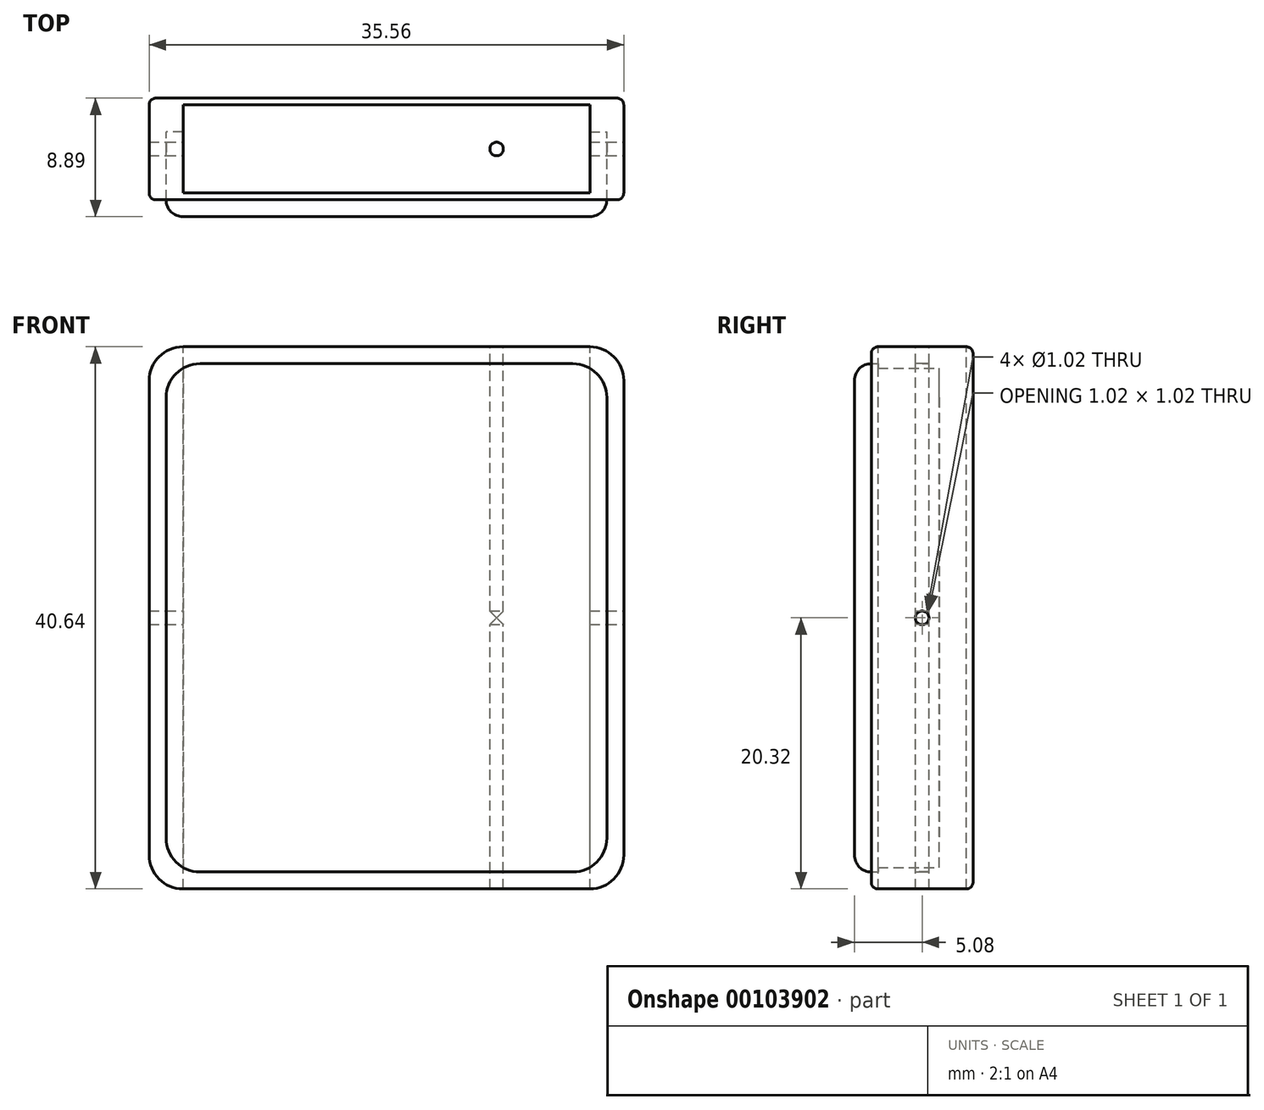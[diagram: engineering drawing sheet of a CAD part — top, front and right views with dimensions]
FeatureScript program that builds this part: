
annotation { "Feature Type Name" : "Feature", "Feature Type Description" : "" }
export const myFeature = defineFeature(function(context is Context, id is Id, definition is map)
    precondition{}
    {
        {
            var Q0;
            Q0=qCreatedBy(makeId("Front.planeOp"),FACE);
            var sketch = newSketch(context, id + "F0", { "sketchPlane" : qUnion([Q0])});
            skLineSegment(sketch, "E0.bottom", {"start": v(-17.78, -20.32) * mm, "end": v(17.78, -20.32) * mm});
            skLineSegment(sketch, "E0.top", {"start": v(-17.78, 20.32) * mm, "end": v(17.78, 20.32) * mm});
            skLineSegment(sketch, "E0.left", {"start": v(-17.78, -20.32) * mm, "end": v(-17.78, 20.32) * mm});
            skLineSegment(sketch, "E0.right", {"start": v(17.78, -20.32) * mm, "end": v(17.78, 20.32) * mm});
            skPoint(sketch, "E0.middle", {"position": v(0, 0) * mm});
            skSolve(sketch);
        }
        {
            var Q0;
            Q0=makeQuery(id+"F0.imprint","IMPRINT",FACE,{"disambiguationData":[TD([[makeQuery(id+"F0.imprint","IMPRINT",EDGE,{"derivedFrom":sQuery(id+"F0.wireOp",EDGE,"E0.bottom")}),1.0]])]});
            extrude(context, id + "F1", {"entities" : qUnion([Q0]), "depth" : 3.8 * mm, "hasSecondDirection" : true, "secondDirectionOppositeDirection" : true, "secondDirectionDepth" : 3.8 * mm});
        }
        {
            var Q0;
            Q0=makeQuery(id+"F1.opExtrude","CAP_FACE",FACE,{"disambiguationData":[OSD([sQuery(id+"F0.wireOp",EDGE,"E0.bottom"),sQuery(id+"F0.wireOp",EDGE,"E0.top"),sQuery(id+"F0.wireOp",EDGE,"E0.left"),sQuery(id+"F0.wireOp",EDGE,"E0.right")])],"isStart":false});
            var sketch = newSketch(context, id + "F2", { "sketchPlane" : qUnion([Q0])});
            skLineSegment(sketch, "E1.bottom", {"start": v(-13.97, 19.05) * mm, "end": v(13.97, 19.05) * mm});
            skLineSegment(sketch, "E1.top", {"start": v(-13.97, -19.05) * mm, "end": v(13.97, -19.05) * mm});
            skLineSegment(sketch, "E1.left", {"start": v(-16.51, 16.51) * mm, "end": v(-16.51, -16.51) * mm});
            skLineSegment(sketch, "E1.right", {"start": v(16.51, 16.51) * mm, "end": v(16.51, -16.51) * mm});
            skPoint(sketch, "E1.middle", {"position": v(0, 0) * mm});
            skPoint(sketch, "E2.visualSharp", {"position": v(16.51, 19.05) * mm});
            skArc(sketch, "E2.filletArc", {"start": v(16.51, 16.51) * mm, "mid": v(15.77, 18.3) * mm, "end": v(13.97, 19.05) * mm});
            skPoint(sketch, "E3.visualSharp", {"position": v(-16.51, 19.05) * mm});
            skArc(sketch, "E3.filletArc", {"start": v(-13.97, 19.05) * mm, "mid": v(-15.77, 18.3) * mm, "end": v(-16.51, 16.51) * mm});
            skPoint(sketch, "E4.visualSharp", {"position": v(-16.51, -19.05) * mm});
            skArc(sketch, "E4.filletArc", {"start": v(-16.51, -16.51) * mm, "mid": v(-15.77, -18.3) * mm, "end": v(-13.97, -19.05) * mm});
            skPoint(sketch, "E5.visualSharp", {"position": v(16.51, -19.05) * mm});
            skArc(sketch, "E5.filletArc", {"start": v(13.97, -19.05) * mm, "mid": v(15.77, -18.3) * mm, "end": v(16.51, -16.51) * mm});
            skSolve(sketch);
        }
        {
            var Q0;
            Q0=makeQuery(id+"F2.imprint","IMPRINT",FACE,{"disambiguationData":[TD([[makeQuery(id+"F2.imprint","IMPRINT",EDGE,{"derivedFrom":sQuery(id+"F2.wireOp",EDGE,"E1.bottom")}),-1.0]])]});
            extrude(context, id + "F3", {"entities" : qUnion([Q0]), "operationType" : NewBodyOperationType.REMOVE, "oppositeDirection" : true, "depth" : 5.08 * mm});
        }
        {
            var Q0;
            Q0=makeQuery(id+"F3.boolean.opBoolean","COPY",FACE,{"derivedFrom":makeQuery(id+"F3.opExtrude","CAP_FACE",FACE,{"disambiguationData":[OSD([sQuery(id+"F2.wireOp",EDGE,"E1.bottom"),sQuery(id+"F2.wireOp",EDGE,"E1.top"),sQuery(id+"F2.wireOp",EDGE,"E1.left"),sQuery(id+"F2.wireOp",EDGE,"E1.right")])],"isStart":false})});
            extrude(context, id + "F4", {"entities" : qUnion([Q0]), "depth" : 6.35 * mm});
        }
        {
            var Q0;
            Q0=makeQuery(id+"F1.opExtrude","SWEPT_EDGE",EDGE,{"disambiguationData":[OSD([sQuery(id+"F0.wireOp",EDGE,"E0.top"),sQuery(id+"F0.wireOp",EDGE,"E0.left")])]});
            var Q1;
            Q1=makeQuery(id+"F1.opExtrude","SWEPT_EDGE",EDGE,{"disambiguationData":[OSD([sQuery(id+"F0.wireOp",EDGE,"E0.top"),sQuery(id+"F0.wireOp",EDGE,"E0.right")])]});
            var Q2;
            Q2=makeQuery(id+"F1.opExtrude","SWEPT_EDGE",EDGE,{"disambiguationData":[OSD([sQuery(id+"F0.wireOp",EDGE,"E0.bottom"),sQuery(id+"F0.wireOp",EDGE,"E0.right")])]});
            var Q3;
            Q3=makeQuery(id+"F1.opExtrude","SWEPT_EDGE",EDGE,{"disambiguationData":[OSD([sQuery(id+"F0.wireOp",EDGE,"E0.bottom"),sQuery(id+"F0.wireOp",EDGE,"E0.left")])]});
            fillet(context, id + "F5", {"entities" : qUnion([Q0, Q1, Q2, Q3]), "radius" : 2.54 * mm, "tangentPropagation" : true, "allowEdgeOverflow" : false});
        }
        {
            var Q0;
            Q0=makeQuery(id+"F1.opExtrude","CAP_EDGE",EDGE,{"disambiguationData":[OSD([sQuery(id+"F0.wireOp",EDGE,"E0.top")])],"isStart":false});
            var Q1;
            {var subQ0=sQuery(id+"F0.wireOp",EDGE,"E0.left");var subQ1=sQuery(id+"F0.wireOp",EDGE,"E0.top");Q1=makeQuery(id+"F5.opFillet","BLEND_EDGE",EDGE,{"blendedFrom":[makeQuery(id+"F1.opExtrude","SWEPT_EDGE",EDGE,{"disambiguationData":[OSD([subQ1,subQ0])]}),makeQuery(id+"F1.opExtrude","CAP_FACE",FACE,{"disambiguationData":[OSD([sQuery(id+"F0.wireOp",EDGE,"E0.bottom"),subQ1,subQ0,sQuery(id+"F0.wireOp",EDGE,"E0.right")])],"isStart":false})],"blendedInto":[makeQuery(id+"F1.opExtrude","CAP_FACE",FACE,{"disambiguationData":[OSD([sQuery(id+"F0.wireOp",EDGE,"E0.bottom"),subQ1,subQ0,sQuery(id+"F0.wireOp",EDGE,"E0.right")])],"isStart":false})]});}
            var Q2;
            Q2=makeQuery(id+"F1.opExtrude","CAP_FACE",FACE,{"disambiguationData":[OSD([sQuery(id+"F0.wireOp",EDGE,"E0.bottom"),sQuery(id+"F0.wireOp",EDGE,"E0.top"),sQuery(id+"F0.wireOp",EDGE,"E0.left"),sQuery(id+"F0.wireOp",EDGE,"E0.right")])],"isStart":true});
            fillet(context, id + "F6", {"entities" : qUnion([Q0, Q1, Q2]), "radius" : 0.5 * mm, "tangentPropagation" : true, "allowEdgeOverflow" : false});
        }
        {
            var Q0;
            Q0=makeQuery(id+"F4.opExtrude","CAP_FACE",FACE,{"disambiguationData":[OSD([sQuery(id+"F2.wireOp",EDGE,"E1.bottom"),sQuery(id+"F2.wireOp",EDGE,"E1.top"),sQuery(id+"F2.wireOp",EDGE,"E1.left"),sQuery(id+"F2.wireOp",EDGE,"E1.right")])],"isStart":false});
            fillet(context, id + "F7", {"entities" : qUnion([Q0]), "radius" : 1.27 * mm, "tangentPropagation" : true, "allowEdgeOverflow" : false});
        }
        {
            var Q0;
            Q0=makeQuery(id+"F1.opExtrude","SWEPT_FACE",FACE,{"disambiguationData":[OSD([sQuery(id+"F0.wireOp",EDGE,"E0.right")])]});
            var sketch = newSketch(context, id + "F8", { "sketchPlane" : qUnion([Q0])});
            skCircle(sketch, "E6", {"center": v(0, 0) * mm, "radius": 0.5 * mm});
            skSolve(sketch);
        }
        {
            var Q0;
            Q0=makeQuery(id+"F8.imprint","IMPRINT",FACE,{"disambiguationData":[TD([[makeQuery(id+"F8.imprint","IMPRINT",EDGE,{"derivedFrom":sQuery(id+"F8.wireOp",EDGE,"E6")}),1.0]])]});
            extrude(context, id + "F9", {"entities" : qUnion([Q0]), "operationType" : NewBodyOperationType.REMOVE, "endBound" : BoundingType.THROUGH_ALL, "oppositeDirection" : true, "depth" : 5.08 * mm});
        }
        {
            var Q0;
            Q0=makeQuery(id+"F1.opExtrude","SWEPT_FACE",FACE,{"disambiguationData":[OSD([sQuery(id+"F0.wireOp",EDGE,"E0.top")])]});
            var sketch = newSketch(context, id + "F10", { "sketchPlane" : qUnion([Q0])});
            skCircle(sketch, "E7", {"center": v(-8.26, 0) * mm, "radius": 0.5 * mm});
            skCircle(sketch, "E8.MirrorC", {"center": v(8.26, 0) * mm, "radius": 0.5 * mm});
            skSolve(sketch);
        }
        {
            var Q0;
            Q0=makeQuery(id+"F10.imprint","IMPRINT",FACE,{"disambiguationData":[TD([[makeQuery(id+"F10.imprint","IMPRINT",EDGE,{"derivedFrom":sQuery(id+"F10.wireOp",EDGE,"E7")}),1.0]])]});
            var Q1;
            Q1=makeQuery(id+"F10.imprint","IMPRINT",FACE,{"disambiguationData":[TD([[makeQuery(id+"F10.imprint","IMPRINT",EDGE,{"derivedFrom":sQuery(id+"F10.wireOp",EDGE,"E8.MirrorC")}),-1.0]])]});
            extrude(context, id + "F11", {"entities" : qUnion([Q0, Q1]), "operationType" : NewBodyOperationType.REMOVE, "endBound" : BoundingType.THROUGH_ALL, "oppositeDirection" : true, "depth" : 25.4 * mm});
        }
    });
